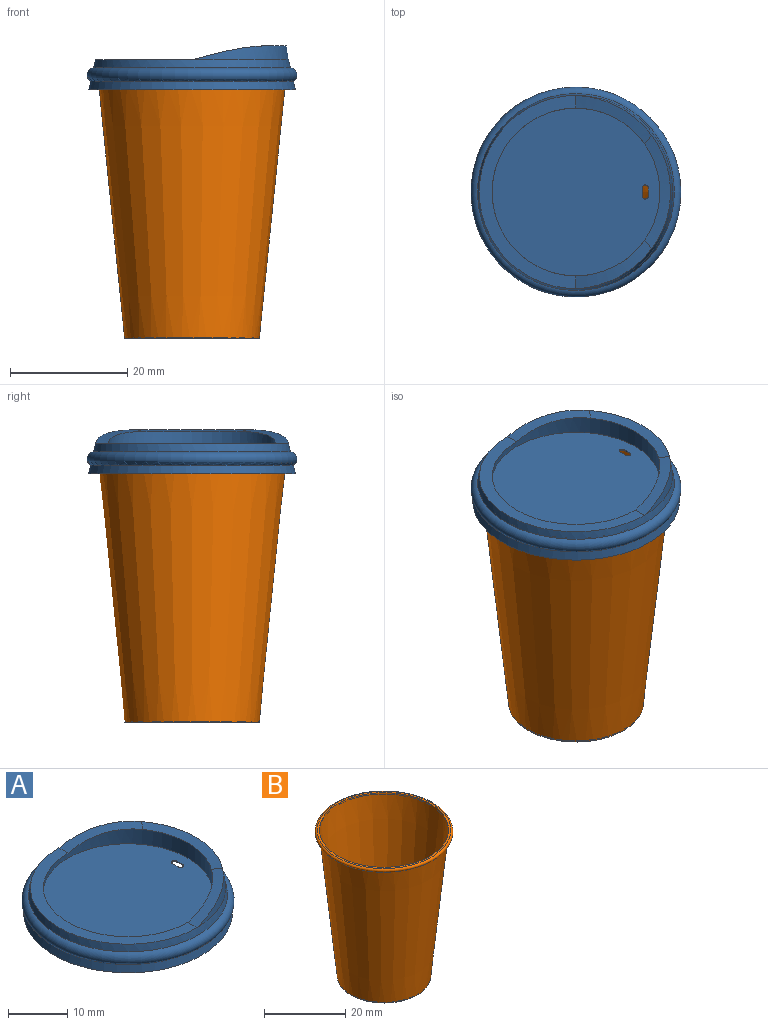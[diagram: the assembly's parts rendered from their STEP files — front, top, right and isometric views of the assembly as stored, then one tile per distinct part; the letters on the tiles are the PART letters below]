
ASSEMBLY  parts=2 mates=1
PART A: 19 faces, bbox 38.8x40.1x8 mm
  f0: plane 33.01x16.51mm, normal (0,0,1), area 105.6mm2, adj f1,f11,f12,f13
  f1: cone r=16.81mm half-angle=12.7deg, axis (0,0,-1), area 146.5mm2, adj f0,f8,f9
  f2: cone r=16.56mm half-angle=90deg, axis (0,0,1), area 859.7mm2, adj f3,f15,f16,f17,f18
  f3: cone r=16.65mm half-angle=12.7deg, axis (0,0,-1), area 39.3mm2, adj f2,f4
  f4: torus R=16.72mm, axis (0,0,1), area 314.6mm2, adj f3,f5
  f5: cone r=17.45mm half-angle=12.7deg, axis (0,0,-1), area 179.6mm2, adj f4,f6
  f6: plane 35.3x35.3mm, normal (0,0,-1), area 22.6mm2, adj f5,f7
  f7: cone r=17.65mm half-angle=12.7deg, axis (0,0,-1), area 169.3mm2, adj f6,f8
  f8: torus R=16.72mm, axis (0,0,1), area 342.5mm2, adj f1,f7
  f9: cone r=16.5mm half-angle=8.2deg, axis (0,0,-1), area 88.1mm2, adj f1,f10,f12,f13
  f10: cone r=16.15mm half-angle=80.7deg, axis (0,0,1), area 35.5mm2, adj f9,f11,f12,f13
  f11: cylinder r=14.32mm len=28.64mm, axis (0,0,1), area 156mm2, adj f0,f10,f12,f13,f14
  f12: bspline ~14.7x13.52mm, area 28.8mm2, adj f0,f9,f10,f11
  f13: bspline ~14.7x13.52mm, area 28.8mm2, adj f0,f9,f10,f11
  f14: plane 28.64x28.64mm, normal (0,0,1), area 641.9mm2, adj f11,f15,f16,f17,f18
  f15: plane 1.4x0.21mm, normal (1,0,0), area 0.3mm2, adj f2,f14,f16,f18
  f16: cylinder r=0.51mm len=1.02mm, axis (0,0,1), area 0.3mm2, adj f2,f14,f15,f17
  f17: plane 1.4x0.21mm, normal (-1,0,0), area 0.3mm2, adj f2,f14,f16,f18
  f18: cylinder r=0.51mm len=1.02mm, axis (0,0,1), area 0.3mm2, adj f2,f14,f15,f17
PART B: 9 faces, bbox 36.7x36.7x44 mm
  f0: cone r=15.95mm half-angle=5.8deg, axis (0,0,1), area 3775.8mm2, adj f1,f8
  f1: torus R=16.45mm, axis (0,0,1), area 250.2mm2, adj f0,f2
  f2: plane 32.9x32.9mm, normal (0,0,1), area 56.1mm2, adj f1,f3
  f3: cone r=15.9mm half-angle=5.8deg, axis (0,0,1), area 3779.6mm2, adj f2,f4
  f4: cone r=11.08mm half-angle=10deg, axis (0,0,-1), area 136.4mm2, adj f3,f5
  f5: plane 22.17x22.17mm, normal (0,0,1), area 386mm2, adj f4
  f6: plane 22x22mm, normal (0,0,-1), area 380.1mm2, adj f7
  f7: cone r=11mm half-angle=10deg, axis (0,0,-1), area 141.9mm2, adj f6,f8
  f8: plane 23x23mm, normal (0,0,-1), area 10.7mm2, adj f0,f7
PLACE A t=(10.89,6.51,0.07)mm
PLACE B t=(10.89,6.51,26.79)mm
MATE slider B.f0 <-> A.f1  axis (0,0,1) through (10.89,6.51,6.96)mm
